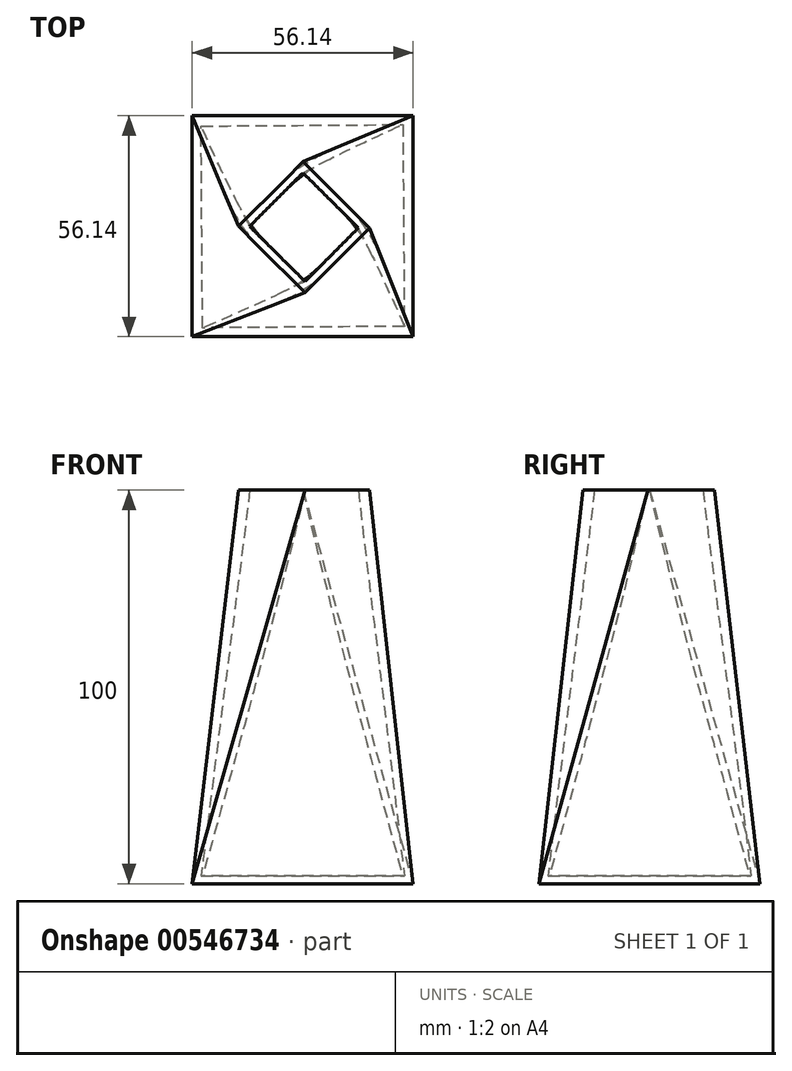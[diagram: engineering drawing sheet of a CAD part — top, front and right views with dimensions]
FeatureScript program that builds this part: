
annotation { "Feature Type Name" : "Feature", "Feature Type Description" : "" }
export const myFeature = defineFeature(function(context is Context, id is Id, definition is map)
    precondition{}
    {
        {
            var Q0;
            Q0=qCreatedBy(makeId("Top.planeOp"),FACE);
            var sketch = newSketch(context, id + "F0", { "sketchPlane" : qUnion([Q0])});
            skLineSegment(sketch, "E0.bottom", {"start": v(28.07, -28.07) * mm, "end": v(-28.07, -28.07) * mm});
            skLineSegment(sketch, "E0.top", {"start": v(28.07, 28.07) * mm, "end": v(-28.07, 28.07) * mm});
            skLineSegment(sketch, "E0.left", {"start": v(28.07, -28.07) * mm, "end": v(28.07, 28.07) * mm});
            skLineSegment(sketch, "E0.right", {"start": v(-28.07, -28.07) * mm, "end": v(-28.07, 28.07) * mm});
            skPoint(sketch, "E0.middle", {"position": v(0, 0) * mm});
            skSolve(sketch);
        }
        {
            var Q0;
            Q0=qCreatedBy(makeId("Top.planeOp"),FACE);
            cPlane(context, id + "F1", {"entities" : qUnion([Q0]), "cplaneType" : CPlaneType.OFFSET, "offset" : 100 * mm, "width" : 150 * mm, "height" : 150 * mm});
        }
        {
            var Q0;
            Q0=qCreatedBy(id+"F1.planeOp",FACE);
            var sketch = newSketch(context, id + "F2", { "sketchPlane" : qUnion([Q0])});
            skLineSegment(sketch, "E1.bottom", {"start": v(0.11, 16.43) * mm, "end": v(-16.31, 0) * mm});
            skLineSegment(sketch, "E1.top", {"start": v(17, -0.47) * mm, "end": v(0.58, -16.9) * mm});
            skLineSegment(sketch, "E1.left", {"start": v(0.11, 16.43) * mm, "end": v(17, -0.47) * mm});
            skLineSegment(sketch, "E1.right", {"start": v(-16.31, 0) * mm, "end": v(0.58, -16.9) * mm});
            skPoint(sketch, "E1.middle", {"position": v(0, 0) * mm});
            skSolve(sketch);
        }
        {
            var Q0;
            Q0=makeQuery(id+"F2.imprint","IMPRINT",FACE,{"disambiguationData":[TD([[makeQuery(id+"F2.imprint","IMPRINT",EDGE,{"derivedFrom":sQuery(id+"F2.wireOp",EDGE,"E1.bottom")}),1.0]])]});
            var Q1;
            Q1=makeQuery(id+"F0.imprint","IMPRINT",FACE,{"disambiguationData":[TD([[makeQuery(id+"F0.imprint","IMPRINT",EDGE,{"derivedFrom":sQuery(id+"F0.wireOp",EDGE,"E0.bottom")}),-1.0]])]});
            loft(context, id + "F3", {"sheetProfilesArray" : [{ "sheetProfileEntities" : qUnion([Q0]) }, { "sheetProfileEntities" : qUnion([Q1]) }]});
        }
        {
            var Q0;
            Q0=makeQuery(id+"F3.opLoft","CAP_FACE",FACE,{"disambiguationData":[OSD([makeQuery(id+"F2.imprint","IMPRINT",FACE,{"disambiguationData":[TD([[makeQuery(id+"F2.imprint","IMPRINT",EDGE,{"derivedFrom":sQuery(id+"F2.wireOp",EDGE,"E1.bottom")}),1.0]])]})])],"isStart":true});
            shell(context, id + "F4", {"entities" : qUnion([Q0]), "thickness" : 2 * mm});
        }
    });
